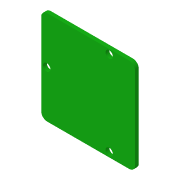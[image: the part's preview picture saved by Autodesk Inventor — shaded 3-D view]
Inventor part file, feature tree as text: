
AUTODESK INVENTOR PART (.ipt)
format: ipt  version: 2018 (Build 220112000, 112)  size: 105,984 bytes
history: native  units: in
note: dims shown in document units (in); Inventor stores cm internally (conversion verified against a paired STEP export)
features: extrude x2, sketch x2, fillet x1
ambient origin geometry x8: Origin, YZ Plane, XZ Plane, XY Plane, X Axis, Y Axis, Z Axis, Center Point
bodies: Solid1 (feature_tree)
feature tree (5):
  extrude  "Extrusion1"  Depth=2.0in
  fillet  "Fillet1"  Radius=2.0in
  extrude  "Extrusion2"  Depth=0.0787in TaperAngle=0.0deg
  sketch  "Sketch1"  dims[d0=1.0in d1=2.0in d2=2.0in]
  sketch  "Sketch2"  dims[d3=1.0in d4=0.0787in d5=0.0in d6=0.125in d7=0.1575in d9=0.1575in d10=0.1575in d11=0.4488in d12=0.9in d13=0.9in d14=0.4488in d15=0.0787in d16=0.0in d17=0.1181in]
